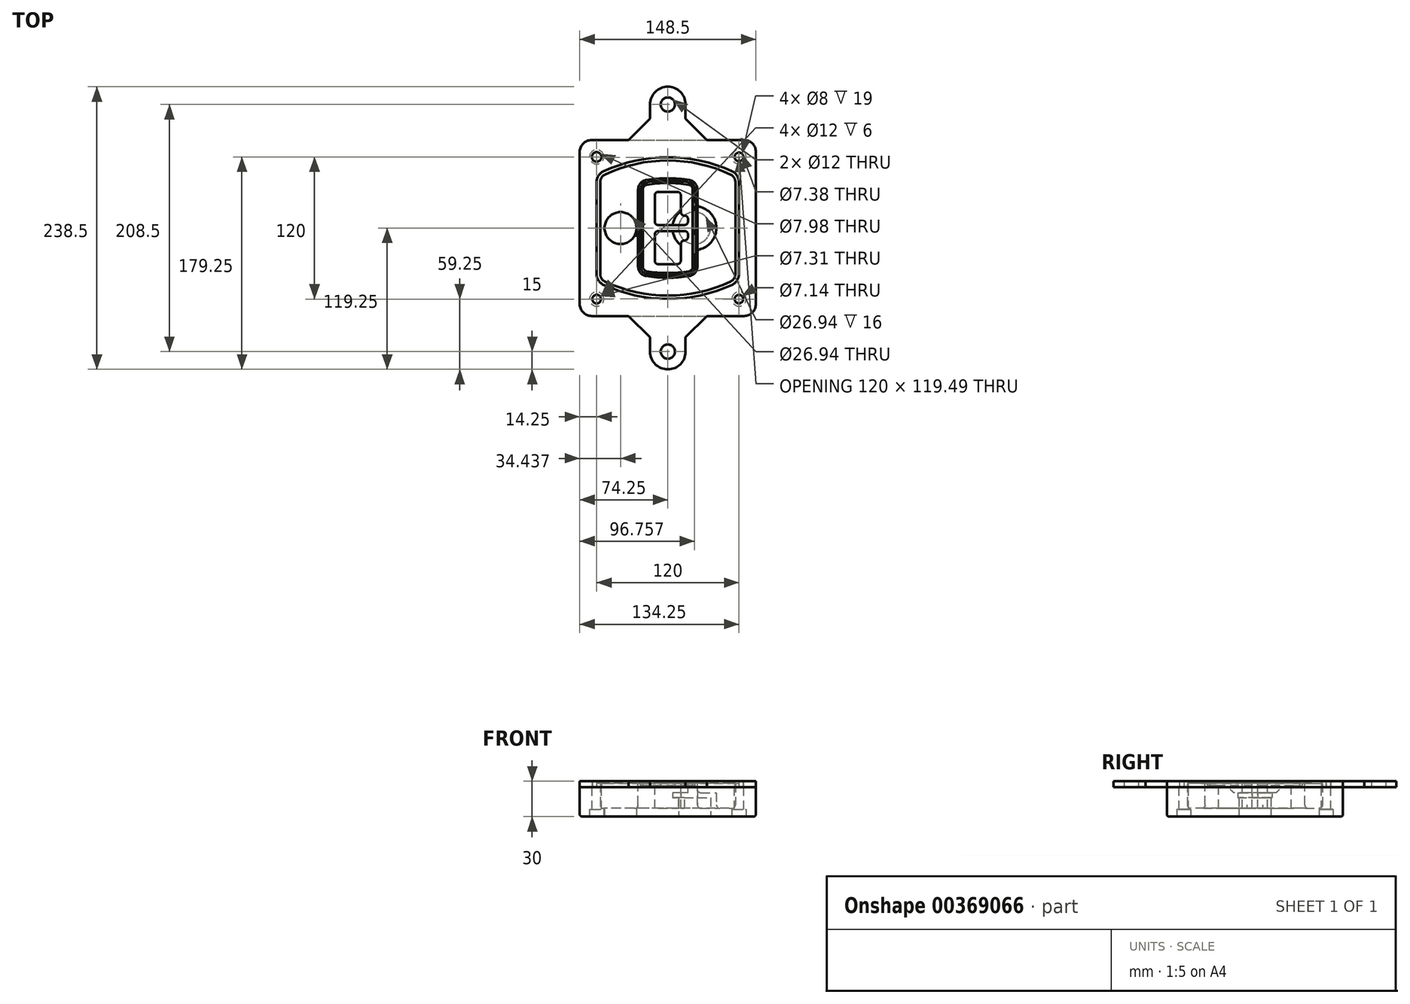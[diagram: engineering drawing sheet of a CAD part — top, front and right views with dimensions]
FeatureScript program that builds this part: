
annotation { "Feature Type Name" : "Feature", "Feature Type Description" : "" }
export const myFeature = defineFeature(function(context is Context, id is Id, definition is map)
    precondition{}
    {
        {
            var Q0;
            Q0=qCreatedBy(makeId("Top.planeOp"),FACE);
            var sketch = newSketch(context, id + "F0", { "sketchPlane" : qUnion([Q0])});
            skPoint(sketch, "E0.rect.middle", {"position": v(0, 0) * mm});
            skLineSegment(sketch, "E1.bottom", {"start": v(-64.25, -74.25) * mm, "end": v(64.25, -74.25) * mm});
            skLineSegment(sketch, "E1.top", {"start": v(-64.25, 74.25) * mm, "end": v(64.25, 74.25) * mm});
            skLineSegment(sketch, "E1.left", {"start": v(-74.25, -64.25) * mm, "end": v(-74.25, 64.25) * mm});
            skLineSegment(sketch, "E1.right", {"start": v(74.25, -64.25) * mm, "end": v(74.25, 64.25) * mm});
            skLineSegment(sketch, "E2", {"start": v(-74.25, 74.25) * mm, "end": v(74.25, -74.25) * mm, "construction": true});
            skLineSegment(sketch, "E3", {"start": v(74.25, 74.25) * mm, "end": v(-74.25, -74.25) * mm, "construction": true});
            skCircle(sketch, "E4", {"center": v(-60, 60) * mm, "radius": 4 * mm});
            skCircle(sketch, "E5", {"center": v(60, 60) * mm, "radius": 4 * mm});
            skCircle(sketch, "E6", {"center": v(60, -60) * mm, "radius": 4 * mm});
            skCircle(sketch, "E7", {"center": v(-60, -60) * mm, "radius": 4 * mm});
            skLineSegment(sketch, "E8", {"start": v(-60, 60) * mm, "end": v(60, 60) * mm, "construction": true});
            skLineSegment(sketch, "E9", {"start": v(60, 60) * mm, "end": v(60, -60) * mm, "construction": true});
            skLineSegment(sketch, "E10", {"start": v(60, -60) * mm, "end": v(-60, -60) * mm, "construction": true});
            skLineSegment(sketch, "E11", {"start": v(-60, -60) * mm, "end": v(-60, 60) * mm, "construction": true});
            skLineSegment(sketch, "E12", {"start": v(-60, 38.83) * mm, "end": v(-60, -38.83) * mm});
            skLineSegment(sketch, "E13", {"start": v(60, 38.83) * mm, "end": v(60, -38.83) * mm});
            skArc(sketch, "E14", {"start": v(54.26, 47.88) * mm, "mid": v(0, 60) * mm, "end": v(-54.26, 47.88) * mm});
            skArc(sketch, "E15", {"start": v(-54.26, -47.88) * mm, "mid": v(0, -60) * mm, "end": v(54.26, -47.88) * mm});
            skLineSegment(sketch, "E16", {"start": v(-60, 0) * mm, "end": v(60, 0) * mm, "construction": true});
            skPoint(sketch, "E17.visualSharp", {"position": v(-60, -45) * mm});
            skArc(sketch, "E17.filletArc", {"start": v(-60, -38.83) * mm, "mid": v(-58.44, -44.2) * mm, "end": v(-54.26, -47.88) * mm});
            skPoint(sketch, "E18.visualSharp", {"position": v(-60, 45) * mm});
            skArc(sketch, "E18.filletArc", {"start": v(-54.26, 47.88) * mm, "mid": v(-58.44, 44.2) * mm, "end": v(-60, 38.83) * mm});
            skPoint(sketch, "E19.visualSharp", {"position": v(60, 45) * mm});
            skArc(sketch, "E19.filletArc", {"start": v(60, 38.83) * mm, "mid": v(58.44, 44.2) * mm, "end": v(54.26, 47.88) * mm});
            skPoint(sketch, "E20.visualSharp", {"position": v(60, -45) * mm});
            skArc(sketch, "E20.filletArc", {"start": v(54.26, -47.88) * mm, "mid": v(58.44, -44.2) * mm, "end": v(60, -38.83) * mm});
            skPoint(sketch, "E21.visualSharp", {"position": v(-74.25, 74.25) * mm});
            skArc(sketch, "E21.filletArc", {"start": v(-64.25, 74.25) * mm, "mid": v(-71.32, 71.32) * mm, "end": v(-74.25, 64.25) * mm});
            skPoint(sketch, "E22.visualSharp", {"position": v(74.25, 74.25) * mm});
            skArc(sketch, "E22.filletArc", {"start": v(74.25, 64.25) * mm, "mid": v(71.32, 71.32) * mm, "end": v(64.25, 74.25) * mm});
            skPoint(sketch, "E23.visualSharp", {"position": v(74.25, -74.25) * mm});
            skArc(sketch, "E23.filletArc", {"start": v(64.25, -74.25) * mm, "mid": v(71.32, -71.32) * mm, "end": v(74.25, -64.25) * mm});
            skPoint(sketch, "E24.visualSharp", {"position": v(-74.25, -74.25) * mm});
            skArc(sketch, "E24.filletArc", {"start": v(-74.25, -64.25) * mm, "mid": v(-71.32, -71.32) * mm, "end": v(-64.25, -74.25) * mm});
            skArc(sketch, "E25.0", {"start": v(57, 38.83) * mm, "mid": v(55.9, 42.58) * mm, "end": v(52.98, 45.17) * mm});
            skLineSegment(sketch, "E25.1", {"start": v(57, 38.83) * mm, "end": v(57, -38.83) * mm});
            skArc(sketch, "E25.2", {"start": v(52.98, -45.17) * mm, "mid": v(55.9, -42.58) * mm, "end": v(57, -38.83) * mm});
            skArc(sketch, "E25.3", {"start": v(-52.98, -45.17) * mm, "mid": v(0, -57) * mm, "end": v(52.98, -45.17) * mm});
            skArc(sketch, "E25.4", {"start": v(-57, -38.83) * mm, "mid": v(-55.9, -42.58) * mm, "end": v(-52.98, -45.17) * mm});
            skArc(sketch, "E25.5", {"start": v(52.98, 45.17) * mm, "mid": v(0, 57) * mm, "end": v(-52.98, 45.17) * mm});
            skLineSegment(sketch, "E25.6", {"start": v(-57, 38.83) * mm, "end": v(-57, -38.83) * mm});
            skArc(sketch, "E25.7", {"start": v(-52.98, 45.17) * mm, "mid": v(-55.9, 42.58) * mm, "end": v(-57, 38.83) * mm});
            skArc(sketch, "E26.0", {"start": v(-55.96, 51.5) * mm, "mid": v(-61.82, 46.33) * mm, "end": v(-64, 38.83) * mm});
            skArc(sketch, "E26.1", {"start": v(55.96, 51.5) * mm, "mid": v(0, 64) * mm, "end": v(-55.96, 51.5) * mm});
            skArc(sketch, "E26.2", {"start": v(64, 38.83) * mm, "mid": v(61.82, 46.33) * mm, "end": v(55.96, 51.5) * mm});
            skLineSegment(sketch, "E26.3", {"start": v(64, 38.83) * mm, "end": v(64, -38.83) * mm});
            skArc(sketch, "E26.4", {"start": v(55.96, -51.5) * mm, "mid": v(61.82, -46.33) * mm, "end": v(64, -38.83) * mm});
            skLineSegment(sketch, "E26.5", {"start": v(-64, 38.83) * mm, "end": v(-64, -38.83) * mm});
            skArc(sketch, "E26.6", {"start": v(-55.96, -51.5) * mm, "mid": v(0, -64) * mm, "end": v(55.96, -51.5) * mm});
            skArc(sketch, "E26.7", {"start": v(-64, -38.83) * mm, "mid": v(-61.82, -46.33) * mm, "end": v(-55.96, -51.5) * mm});
            skSolve(sketch);
        }
        {
            var Q0;
            Q0=makeQuery(id+"F0.imprint","IMPRINT",FACE,{"disambiguationData":[TD([[makeQuery(id+"F0.imprint","IMPRINT",EDGE,{"derivedFrom":sQuery(id+"F0.wireOp",EDGE,"E1.bottom")}),1.0]])]});
            var Q1;
            Q1=makeQuery(id+"F0.imprint","IMPRINT",FACE,{"disambiguationData":[TD([[makeQuery(id+"F0.imprint","IMPRINT",EDGE,{"derivedFrom":sQuery(id+"F0.wireOp",EDGE,"E12")}),1.0]])]});
            var Q2;
            Q2=makeQuery(id+"F0.imprint","IMPRINT",FACE,{"disambiguationData":[TD([[makeQuery(id+"F0.imprint","IMPRINT",EDGE,{"derivedFrom":sQuery(id+"F0.wireOp",EDGE,"E25.0")}),1.0]])]});
            var Q3;
            Q3=makeQuery(id+"F0.imprint","IMPRINT",FACE,{"disambiguationData":[TD([[makeQuery(id+"F0.imprint","IMPRINT",EDGE,{"derivedFrom":sQuery(id+"F0.wireOp",EDGE,"E12")}),-1.0]])]});
            extrude(context, id + "F1", {"entities" : qUnion([Q0, Q1, Q2, Q3]), "oppositeDirection" : true, "depth" : 25 * mm});
        }
        {
            var Q0;
            Q0=makeQuery(id+"F0.imprint","IMPRINT",FACE,{"disambiguationData":[TD([[makeQuery(id+"F0.imprint","IMPRINT",EDGE,{"derivedFrom":sQuery(id+"F0.wireOp",EDGE,"E12")}),1.0]])]});
            extrude(context, id + "F2", {"entities" : qUnion([Q0]), "operationType" : NewBodyOperationType.ADD, "depth" : 3 * mm});
        }
        {
            var Q0;
            Q0=makeQuery(id+"F0.imprint","IMPRINT",FACE,{"disambiguationData":[TD([[makeQuery(id+"F0.imprint","IMPRINT",EDGE,{"derivedFrom":sQuery(id+"F0.wireOp",EDGE,"E25.0")}),1.0]])]});
            extrude(context, id + "F3", {"entities" : qUnion([Q0]), "operationType" : NewBodyOperationType.REMOVE, "oppositeDirection" : true, "depth" : 18 * mm});
        }
        {
            var Q0;
            Q0=makeQuery(id+"F2.opExtrude","CAP_FACE",FACE,{"disambiguationData":[OSD([sQuery(id+"F0.wireOp",EDGE,"E12"),sQuery(id+"F0.wireOp",EDGE,"E13"),sQuery(id+"F0.wireOp",EDGE,"E14"),sQuery(id+"F0.wireOp",EDGE,"E15"),sQuery(id+"F0.wireOp",EDGE,"E17.filletArc"),sQuery(id+"F0.wireOp",EDGE,"E18.filletArc"),sQuery(id+"F0.wireOp",EDGE,"E19.filletArc"),sQuery(id+"F0.wireOp",EDGE,"E20.filletArc"),sQuery(id+"F0.wireOp",EDGE,"E25.0"),sQuery(id+"F0.wireOp",EDGE,"E25.1"),sQuery(id+"F0.wireOp",EDGE,"E25.2"),sQuery(id+"F0.wireOp",EDGE,"E25.3"),sQuery(id+"F0.wireOp",EDGE,"E25.4"),sQuery(id+"F0.wireOp",EDGE,"E25.5"),sQuery(id+"F0.wireOp",EDGE,"E25.6"),sQuery(id+"F0.wireOp",EDGE,"E25.7")])],"isStart":false});
            var sketch = newSketch(context, id + "F4", { "sketchPlane" : qUnion([Q0])});
            skArc(sketch, "E27.0", {"start": v(-18.34, -40.45) * mm, "mid": v(0, -42) * mm, "end": v(18.34, -40.45) * mm});
            skArc(sketch, "E28.0", {"start": v(18.34, 40.45) * mm, "mid": v(0, 42) * mm, "end": v(-18.34, 40.45) * mm});
            skLineSegment(sketch, "E29", {"start": v(-25, 32.57) * mm, "end": v(-25, -32.57) * mm});
            skLineSegment(sketch, "E30", {"start": v(25, 32.57) * mm, "end": v(25, -32.57) * mm});
            skLineSegment(sketch, "E31", {"start": v(-25, 39.1) * mm, "end": v(25, 39.1) * mm, "construction": true});
            skLineSegment(sketch, "E32", {"start": v(-25, -39.1) * mm, "end": v(25, -39.1) * mm, "construction": true});
            skPoint(sketch, "E33.visualSharp", {"position": v(-25, 39.1) * mm});
            skArc(sketch, "E33.filletArc", {"start": v(-18.34, 40.45) * mm, "mid": v(-23.11, 37.73) * mm, "end": v(-25, 32.57) * mm});
            skPoint(sketch, "E34.visualSharp", {"position": v(25, 39.1) * mm});
            skArc(sketch, "E34.filletArc", {"start": v(25, 32.57) * mm, "mid": v(23.11, 37.73) * mm, "end": v(18.34, 40.45) * mm});
            skPoint(sketch, "E35.visualSharp", {"position": v(25, -39.1) * mm});
            skArc(sketch, "E35.filletArc", {"start": v(18.34, -40.45) * mm, "mid": v(23.11, -37.73) * mm, "end": v(25, -32.57) * mm});
            skPoint(sketch, "E36.visualSharp", {"position": v(-25, -39.1) * mm});
            skArc(sketch, "E36.filletArc", {"start": v(-25, -32.57) * mm, "mid": v(-23.11, -37.73) * mm, "end": v(-18.34, -40.45) * mm});
            skArc(sketch, "E37.0", {"start": v(52.98, 45.17) * mm, "mid": v(0, 57) * mm, "end": v(-52.98, 45.17) * mm});
            skArc(sketch, "E37.1", {"start": v(-52.98, 45.17) * mm, "mid": v(-55.9, 42.58) * mm, "end": v(-57, 38.83) * mm});
            skLineSegment(sketch, "E37.2", {"start": v(-57, 38.83) * mm, "end": v(-57, -38.83) * mm});
            skArc(sketch, "E37.3", {"start": v(-57, -38.83) * mm, "mid": v(-55.9, -42.58) * mm, "end": v(-52.98, -45.17) * mm});
            skArc(sketch, "E37.4", {"start": v(-52.98, -45.17) * mm, "mid": v(0, -57) * mm, "end": v(52.98, -45.17) * mm});
            skArc(sketch, "E37.5", {"start": v(52.98, -45.17) * mm, "mid": v(55.9, -42.58) * mm, "end": v(57, -38.83) * mm});
            skLineSegment(sketch, "E37.6", {"start": v(57, 38.83) * mm, "end": v(57, -38.83) * mm});
            skArc(sketch, "E37.7", {"start": v(57, 38.83) * mm, "mid": v(55.9, 42.58) * mm, "end": v(52.98, 45.17) * mm});
            skLineSegment(sketch, "E38.0", {"start": v(23, 32.57) * mm, "end": v(23, -32.57) * mm});
            skArc(sketch, "E38.1", {"start": v(18, -38.48) * mm, "mid": v(21.58, -36.44) * mm, "end": v(23, -32.57) * mm});
            skArc(sketch, "E38.2", {"start": v(-18, -38.48) * mm, "mid": v(0, -40) * mm, "end": v(18, -38.48) * mm});
            skArc(sketch, "E38.3", {"start": v(-23, -32.57) * mm, "mid": v(-21.58, -36.44) * mm, "end": v(-18, -38.48) * mm});
            skLineSegment(sketch, "E38.4", {"start": v(-23, 32.57) * mm, "end": v(-23, -32.57) * mm});
            skArc(sketch, "E38.5", {"start": v(23, 32.57) * mm, "mid": v(21.58, 36.44) * mm, "end": v(18, 38.48) * mm});
            skArc(sketch, "E38.6", {"start": v(-18, 38.48) * mm, "mid": v(-21.58, 36.44) * mm, "end": v(-23, 32.57) * mm});
            skArc(sketch, "E38.7", {"start": v(18, 38.48) * mm, "mid": v(0, 40) * mm, "end": v(-18, 38.48) * mm});
            skArc(sketch, "E39.0", {"start": v(21, 32.57) * mm, "mid": v(20.06, 35.15) * mm, "end": v(17.67, 36.5) * mm});
            skLineSegment(sketch, "E39.1", {"start": v(21, 32.57) * mm, "end": v(21, -32.57) * mm});
            skArc(sketch, "E39.2", {"start": v(17.67, -36.5) * mm, "mid": v(20.06, -35.15) * mm, "end": v(21, -32.57) * mm});
            skArc(sketch, "E39.3", {"start": v(-17.67, -36.5) * mm, "mid": v(0, -38) * mm, "end": v(17.67, -36.5) * mm});
            skArc(sketch, "E39.4", {"start": v(-21, -32.57) * mm, "mid": v(-20.06, -35.15) * mm, "end": v(-17.67, -36.5) * mm});
            skArc(sketch, "E39.5", {"start": v(17.67, 36.5) * mm, "mid": v(0, 38) * mm, "end": v(-17.67, 36.5) * mm});
            skLineSegment(sketch, "E39.6", {"start": v(-21, 32.57) * mm, "end": v(-21, -32.57) * mm});
            skArc(sketch, "E39.7", {"start": v(-17.67, 36.5) * mm, "mid": v(-20.06, 35.15) * mm, "end": v(-21, 32.57) * mm});
            skLineSegment(sketch, "E40", {"start": v(-25, 0) * mm, "end": v(25, 0) * mm, "construction": true});
            skLineSegment(sketch, "E41", {"start": v(-11, 5.5) * mm, "end": v(-11, 27.5) * mm});
            skLineSegment(sketch, "E42", {"start": v(-8, 30.5) * mm, "end": v(8, 30.5) * mm});
            skLineSegment(sketch, "E43", {"start": v(11, 27.5) * mm, "end": v(11, 13.5) * mm});
            skLineSegment(sketch, "E44", {"start": v(14, 10.5) * mm, "end": v(14, 10.5) * mm});
            skLineSegment(sketch, "E45", {"start": v(17, 7.5) * mm, "end": v(17, 5.5) * mm});
            skLineSegment(sketch, "E46", {"start": v(14, 2.5) * mm, "end": v(-8, 2.5) * mm});
            skPoint(sketch, "E47.visualSharp", {"position": v(-11, 30.5) * mm});
            skArc(sketch, "E47.filletArc", {"start": v(-8, 30.5) * mm, "mid": v(-10.12, 29.62) * mm, "end": v(-11, 27.5) * mm});
            skPoint(sketch, "E48.visualSharp", {"position": v(11, 30.5) * mm});
            skArc(sketch, "E48.filletArc", {"start": v(11, 27.5) * mm, "mid": v(10.12, 29.62) * mm, "end": v(8, 30.5) * mm});
            skPoint(sketch, "E49.visualSharp", {"position": v(11, 10.5) * mm});
            skArc(sketch, "E49.filletArc", {"start": v(11, 13.5) * mm, "mid": v(11.88, 11.38) * mm, "end": v(14, 10.5) * mm});
            skPoint(sketch, "E50.visualSharp", {"position": v(17, 10.5) * mm});
            skArc(sketch, "E50.filletArc", {"start": v(17, 7.5) * mm, "mid": v(16.12, 9.62) * mm, "end": v(14, 10.5) * mm});
            skPoint(sketch, "E51.visualSharp", {"position": v(17, 2.5) * mm});
            skArc(sketch, "E51.filletArc", {"start": v(14, 2.5) * mm, "mid": v(16.12, 3.38) * mm, "end": v(17, 5.5) * mm});
            skPoint(sketch, "E52.visualSharp", {"position": v(-11, 2.5) * mm});
            skArc(sketch, "E52.filletArc", {"start": v(-11, 5.5) * mm, "mid": v(-10.12, 3.38) * mm, "end": v(-8, 2.5) * mm});
            skLineSegment(sketch, "E53.0.MirrorCS", {"start": v(14, -2.5) * mm, "end": v(-8, -2.5) * mm});
            skArc(sketch, "E54.0.MirrorCS", {"start": v(-11, -5.5) * mm, "mid": v(-10.12, -3.38) * mm, "end": v(-8, -2.5) * mm});
            skLineSegment(sketch, "E55.0.MirrorCS", {"start": v(-11, -5.5) * mm, "end": v(-11, -27.5) * mm});
            skArc(sketch, "E56.0.MirrorCS", {"start": v(-8, -30.5) * mm, "mid": v(-10.12, -29.62) * mm, "end": v(-11, -27.5) * mm});
            skLineSegment(sketch, "E57.0.MirrorCS", {"start": v(-8, -30.5) * mm, "end": v(8, -30.5) * mm});
            skArc(sketch, "E58.0.MirrorCS", {"start": v(11, -27.5) * mm, "mid": v(10.12, -29.62) * mm, "end": v(8, -30.5) * mm});
            skLineSegment(sketch, "E59.0.MirrorCS", {"start": v(11, -27.5) * mm, "end": v(11, -13.5) * mm});
            skArc(sketch, "E60.0.MirrorCS", {"start": v(11, -13.5) * mm, "mid": v(11.88, -11.38) * mm, "end": v(14, -10.5) * mm});
            skArc(sketch, "E61.0.MirrorCS", {"start": v(17, -7.5) * mm, "mid": v(16.12, -9.62) * mm, "end": v(14, -10.5) * mm});
            skLineSegment(sketch, "E62.0.MirrorCS", {"start": v(17, -7.5) * mm, "end": v(17, -5.5) * mm});
            skArc(sketch, "E63.0.MirrorCS", {"start": v(14, -2.5) * mm, "mid": v(16.12, -3.38) * mm, "end": v(17, -5.5) * mm});
            skSolve(sketch);
        }
        {
            var Q0;
            Q0=makeQuery(id+"F4.imprint","IMPRINT",FACE,{"disambiguationData":[TD([[makeQuery(id+"F4.imprint","IMPRINT",EDGE,{"derivedFrom":sQuery(id+"F4.wireOp",EDGE,"E27.0")}),1.0]])]});
            var Q1;
            Q1=makeQuery(id+"F4.imprint","IMPRINT",FACE,{"disambiguationData":[TD([[makeQuery(id+"F4.imprint","IMPRINT",EDGE,{"derivedFrom":sQuery(id+"F4.wireOp",EDGE,"E38.0")}),-1.0]])]});
            var Q2;
            Q2=makeQuery(id+"F4.imprint","IMPRINT",FACE,{"disambiguationData":[TD([[makeQuery(id+"F4.imprint","IMPRINT",EDGE,{"derivedFrom":sQuery(id+"F4.wireOp",EDGE,"E39.0")}),1.0]])]});
            extrude(context, id + "F5", {"entities" : qUnion([Q0, Q1, Q2]), "operationType" : NewBodyOperationType.ADD, "endBound" : BoundingType.UP_TO_NEXT, "oppositeDirection" : true, "depth" : 25 * mm});
        }
        {
            var Q0;
            Q0=makeQuery(id+"F4.imprint","IMPRINT",FACE,{"disambiguationData":[TD([[makeQuery(id+"F4.imprint","IMPRINT",EDGE,{"derivedFrom":sQuery(id+"F4.wireOp",EDGE,"E38.0")}),-1.0]])]});
            extrude(context, id + "F6", {"entities" : qUnion([Q0]), "operationType" : NewBodyOperationType.REMOVE, "oppositeDirection" : true, "depth" : 2 * mm});
        }
        {
            var Q0;
            Q0=makeQuery(id+"F1.opExtrude","CAP_FACE",FACE,{"disambiguationData":[OSD([sQuery(id+"F0.wireOp",EDGE,"E1.bottom"),sQuery(id+"F0.wireOp",EDGE,"E1.top"),sQuery(id+"F0.wireOp",EDGE,"E1.left"),sQuery(id+"F0.wireOp",EDGE,"E1.right"),sQuery(id+"F0.wireOp",EDGE,"E4"),sQuery(id+"F0.wireOp",EDGE,"E5"),sQuery(id+"F0.wireOp",EDGE,"E6"),sQuery(id+"F0.wireOp",EDGE,"E7"),sQuery(id+"F0.wireOp",EDGE,"E21.filletArc"),sQuery(id+"F0.wireOp",EDGE,"E22.filletArc"),sQuery(id+"F0.wireOp",EDGE,"E23.filletArc"),sQuery(id+"F0.wireOp",EDGE,"E24.filletArc")])],"isStart":false});
            var sketch = newSketch(context, id + "F7", { "sketchPlane" : qUnion([Q0])});
            skCircle(sketch, "E64", {"center": v(22.5, 0) * mm, "radius": 13.47 * mm});
            skCircle(sketch, "E65", {"center": v(-39.81, 0) * mm, "radius": 13.47 * mm});
            skLineSegment(sketch, "E66", {"start": v(74.25, 0) * mm, "end": v(-74.25, 0) * mm});
            skCircle(sketch, "E67", {"center": v(22.5, 0) * mm, "radius": 18.47 * mm});
            skCircle(sketch, "E68", {"center": v(60, -60) * mm, "radius": 6 * mm});
            skCircle(sketch, "E69", {"center": v(-60, -60) * mm, "radius": 6 * mm});
            skCircle(sketch, "E70", {"center": v(-60, 60) * mm, "radius": 6 * mm});
            skCircle(sketch, "E71", {"center": v(60, 60) * mm, "radius": 6 * mm});
            skSolve(sketch);
        }
        {
            var Q0;
            {var subQ1=sQuery(id+"F7.wireOp",EDGE,"E66");var subQ4=sQuery(id+"F7.wireOp",EDGE,"E64");var subQ6=makeQuery(id+"F7.imprint","INTERSECT",VERTEX,{"disambiguationData":[OD(0.0)],"derivedFrom":[subQ4,subQ1]});Q0=makeQuery(id+"F7.imprint","IMPRINT",FACE,{"disambiguationData":[TD([[makeQuery(id+"F7.imprint","IMPRINT",EDGE,{"disambiguationData":[TD([[subQ6,-1.0]])],"derivedFrom":subQ4}),-1.0]])]});}
            var Q1;
            {var subQ0=sQuery(id+"F7.wireOp",EDGE,"E66");var subQ1=sQuery(id+"F7.wireOp",EDGE,"E64");var subQ3=makeQuery(id+"F7.imprint","INTERSECT",VERTEX,{"disambiguationData":[OD(0.0)],"derivedFrom":[subQ1,subQ0]});Q1=makeQuery(id+"F7.imprint","IMPRINT",FACE,{"disambiguationData":[TD([[makeQuery(id+"F7.imprint","IMPRINT",EDGE,{"disambiguationData":[TD([[subQ3,-1.0]])],"derivedFrom":subQ1}),1.0]])]});}
            var Q2;
            {var subQ0=sQuery(id+"F7.wireOp",EDGE,"E66");var subQ1=sQuery(id+"F7.wireOp",EDGE,"E64");var subQ3=makeQuery(id+"F7.imprint","INTERSECT",VERTEX,{"disambiguationData":[OD(0.0)],"derivedFrom":[subQ1,subQ0]});Q2=makeQuery(id+"F7.imprint","IMPRINT",FACE,{"disambiguationData":[TD([[makeQuery(id+"F7.imprint","IMPRINT",EDGE,{"disambiguationData":[TD([[subQ3,1.0]])],"derivedFrom":subQ1}),1.0]])]});}
            var Q3;
            {var subQ1=sQuery(id+"F7.wireOp",EDGE,"E66");var subQ4=sQuery(id+"F7.wireOp",EDGE,"E64");var subQ6=makeQuery(id+"F7.imprint","INTERSECT",VERTEX,{"disambiguationData":[OD(0.0)],"derivedFrom":[subQ4,subQ1]});Q3=makeQuery(id+"F7.imprint","IMPRINT",FACE,{"disambiguationData":[TD([[makeQuery(id+"F7.imprint","IMPRINT",EDGE,{"disambiguationData":[TD([[subQ6,1.0]])],"derivedFrom":subQ4}),-1.0]])]});}
            extrude(context, id + "F8", {"entities" : qUnion([Q0, Q1, Q2, Q3]), "operationType" : NewBodyOperationType.ADD, "oppositeDirection" : true, "depth" : 20 * mm});
        }
        {
            var Q0;
            {var subQ0=sQuery(id+"F7.wireOp",EDGE,"E66");var subQ1=sQuery(id+"F7.wireOp",EDGE,"E64");var subQ3=makeQuery(id+"F7.imprint","INTERSECT",VERTEX,{"disambiguationData":[OD(0.0)],"derivedFrom":[subQ1,subQ0]});Q0=makeQuery(id+"F7.imprint","IMPRINT",FACE,{"disambiguationData":[TD([[makeQuery(id+"F7.imprint","IMPRINT",EDGE,{"disambiguationData":[TD([[subQ3,-1.0]])],"derivedFrom":subQ1}),1.0]])]});}
            var Q1;
            {var subQ0=sQuery(id+"F7.wireOp",EDGE,"E66");var subQ1=sQuery(id+"F7.wireOp",EDGE,"E64");var subQ3=makeQuery(id+"F7.imprint","INTERSECT",VERTEX,{"disambiguationData":[OD(0.0)],"derivedFrom":[subQ1,subQ0]});Q1=makeQuery(id+"F7.imprint","IMPRINT",FACE,{"disambiguationData":[TD([[makeQuery(id+"F7.imprint","IMPRINT",EDGE,{"disambiguationData":[TD([[subQ3,1.0]])],"derivedFrom":subQ1}),1.0]])]});}
            extrude(context, id + "F9", {"entities" : qUnion([Q0, Q1]), "operationType" : NewBodyOperationType.REMOVE, "oppositeDirection" : true, "depth" : 16 * mm});
        }
        {
            var Q0;
            {var subQ0=sQuery(id+"F7.wireOp",EDGE,"E66");var subQ1=sQuery(id+"F7.wireOp",EDGE,"E65");var subQ3=makeQuery(id+"F7.imprint","INTERSECT",VERTEX,{"disambiguationData":[OD(0.0)],"derivedFrom":[subQ1,subQ0]});Q0=makeQuery(id+"F7.imprint","IMPRINT",FACE,{"disambiguationData":[TD([[makeQuery(id+"F7.imprint","IMPRINT",EDGE,{"disambiguationData":[TD([[subQ3,-1.0]])],"derivedFrom":subQ1}),1.0]])]});}
            var Q1;
            {var subQ0=sQuery(id+"F7.wireOp",EDGE,"E66");var subQ1=sQuery(id+"F7.wireOp",EDGE,"E65");var subQ3=makeQuery(id+"F7.imprint","INTERSECT",VERTEX,{"disambiguationData":[OD(0.0)],"derivedFrom":[subQ1,subQ0]});Q1=makeQuery(id+"F7.imprint","IMPRINT",FACE,{"disambiguationData":[TD([[makeQuery(id+"F7.imprint","IMPRINT",EDGE,{"disambiguationData":[TD([[subQ3,1.0]])],"derivedFrom":subQ1}),1.0]])]});}
            extrude(context, id + "F10", {"entities" : qUnion([Q0, Q1]), "operationType" : NewBodyOperationType.REMOVE, "oppositeDirection" : true, "depth" : 25 * mm});
        }
        {
            var Q0;
            Q0=makeQuery(id+"F7.imprint","IMPRINT",FACE,{"disambiguationData":[TD([[makeQuery(id+"F7.imprint","IMPRINT",EDGE,{"derivedFrom":sQuery(id+"F7.wireOp",EDGE,"E68")}),1.0]])]});
            var Q1;
            Q1=makeQuery(id+"F7.imprint","IMPRINT",FACE,{"disambiguationData":[TD([[makeQuery(id+"F7.imprint","IMPRINT",EDGE,{"derivedFrom":makeQuery(id+"F1.opExtrude","CAP_EDGE",EDGE,{"disambiguationData":[OSD([sQuery(id+"F0.wireOp",EDGE,"E5")])],"isStart":false})}),-1.0]])]});
            var Q2;
            Q2=makeQuery(id+"F7.imprint","IMPRINT",FACE,{"disambiguationData":[TD([[makeQuery(id+"F7.imprint","IMPRINT",EDGE,{"derivedFrom":sQuery(id+"F7.wireOp",EDGE,"E69")}),1.0]])]});
            var Q3;
            Q3=makeQuery(id+"F7.imprint","IMPRINT",FACE,{"disambiguationData":[TD([[makeQuery(id+"F7.imprint","IMPRINT",EDGE,{"derivedFrom":makeQuery(id+"F1.opExtrude","CAP_EDGE",EDGE,{"disambiguationData":[OSD([sQuery(id+"F0.wireOp",EDGE,"E4")])],"isStart":false})}),-1.0]])]});
            var Q4;
            Q4=makeQuery(id+"F7.imprint","IMPRINT",FACE,{"disambiguationData":[TD([[makeQuery(id+"F7.imprint","IMPRINT",EDGE,{"derivedFrom":sQuery(id+"F7.wireOp",EDGE,"E70")}),1.0]])]});
            var Q5;
            Q5=makeQuery(id+"F7.imprint","IMPRINT",FACE,{"disambiguationData":[TD([[makeQuery(id+"F7.imprint","IMPRINT",EDGE,{"derivedFrom":makeQuery(id+"F1.opExtrude","CAP_EDGE",EDGE,{"disambiguationData":[OSD([sQuery(id+"F0.wireOp",EDGE,"E7")])],"isStart":false})}),-1.0]])]});
            var Q6;
            Q6=makeQuery(id+"F7.imprint","IMPRINT",FACE,{"disambiguationData":[TD([[makeQuery(id+"F7.imprint","IMPRINT",EDGE,{"derivedFrom":sQuery(id+"F7.wireOp",EDGE,"E71")}),1.0]])]});
            var Q7;
            Q7=makeQuery(id+"F7.imprint","IMPRINT",FACE,{"disambiguationData":[TD([[makeQuery(id+"F7.imprint","IMPRINT",EDGE,{"derivedFrom":makeQuery(id+"F1.opExtrude","CAP_EDGE",EDGE,{"disambiguationData":[OSD([sQuery(id+"F0.wireOp",EDGE,"E6")])],"isStart":false})}),-1.0]])]});
            extrude(context, id + "F11", {"entities" : qUnion([Q0, Q1, Q2, Q3, Q4, Q5, Q6, Q7]), "operationType" : NewBodyOperationType.REMOVE, "oppositeDirection" : true, "depth" : 6 * mm});
        }
        {
            var Q0;
            Q0=makeQuery(id+"F9.boolean.opBoolean","COPY",FACE,{"derivedFrom":makeQuery(id+"F9.opExtrude","CAP_FACE",FACE,{"disambiguationData":[OSD([sQuery(id+"F7.wireOp",EDGE,"E64")])],"isStart":false})});
            var sketch = newSketch(context, id + "F12", { "sketchPlane" : qUnion([Q0])});
            skArc(sketch, "E72.0", {"start": v(11, 14.45) * mm, "mid": v(6.45, 9.13) * mm, "end": v(4.2, 2.5) * mm});
            skArc(sketch, "E72.1", {"start": v(4.2, -2.5) * mm, "mid": v(6.45, -9.13) * mm, "end": v(11, -14.45) * mm});
            skLineSegment(sketch, "E73", {"start": v(4.2, -2.5) * mm, "end": v(14, -2.5) * mm});
            skLineSegment(sketch, "E74.0", {"start": v(14, 2.5) * mm, "end": v(4.2, 2.5) * mm});
            skArc(sketch, "E74.1", {"start": v(14, 2.5) * mm, "mid": v(16.12, 3.38) * mm, "end": v(17, 5.5) * mm});
            skLineSegment(sketch, "E74.2", {"start": v(17, 7.5) * mm, "end": v(17, 5.5) * mm});
            skArc(sketch, "E74.3", {"start": v(17, 7.5) * mm, "mid": v(16.12, 9.62) * mm, "end": v(14, 10.5) * mm});
            skArc(sketch, "E74.4", {"start": v(11, 13.5) * mm, "mid": v(11.88, 11.38) * mm, "end": v(14, 10.5) * mm});
            skLineSegment(sketch, "E74.5", {"start": v(11, 14.45) * mm, "end": v(11, 13.5) * mm});
            skLineSegment(sketch, "E74.7", {"start": v(14, -2.5) * mm, "end": v(4.2, -2.5) * mm});
            skArc(sketch, "E74.8", {"start": v(14, -2.5) * mm, "mid": v(16.12, -3.38) * mm, "end": v(17, -5.5) * mm});
            skLineSegment(sketch, "E74.9", {"start": v(17, -7.5) * mm, "end": v(17, -5.5) * mm});
            skArc(sketch, "E74.10", {"start": v(17, -7.5) * mm, "mid": v(16.12, -9.62) * mm, "end": v(14, -10.5) * mm});
            skArc(sketch, "E74.11", {"start": v(11, -13.5) * mm, "mid": v(11.88, -11.38) * mm, "end": v(14, -10.5) * mm});
            skLineSegment(sketch, "E74.12", {"start": v(11, -14.45) * mm, "end": v(11, -13.5) * mm});
            skPoint(sketch, "E75.orphan", {"position": v(11, -27.5) * mm});
            skPoint(sketch, "E76.orphan", {"position": v(-8, -2.5) * mm});
            skPoint(sketch, "E77.orphan", {"position": v(-8, 2.5) * mm});
            skPoint(sketch, "E78.orphan", {"position": v(11, 27.5) * mm});
            skSolve(sketch);
        }
        {
            var Q0;
            {var subQ7=sQuery(id+"F12.wireOp",EDGE,"E72.0");var subQ14=sQuery(id+"F12.wireOp",EDGE,"E72.1");var subQ16=sQuery(id+"F12.wireOp",EDGE,"E74.1");var subQ18=sQuery(id+"F12.wireOp",EDGE,"E74.8");Q0=qUnion([makeQuery(id+"F12.imprint","IMPRINT",FACE,{"disambiguationData":[TD([[makeQuery(id+"F12.imprint","IMPRINT",EDGE,{"derivedFrom":subQ7}),1.0]])]}),makeQuery(id+"F12.imprint","IMPRINT",FACE,{"disambiguationData":[TD([[makeQuery(id+"F12.imprint","IMPRINT",EDGE,{"derivedFrom":subQ14}),1.0]])]}),makeQuery(id+"F12.imprint","IMPRINT",FACE,{"disambiguationData":[TD([[makeQuery(id+"F12.imprint","IMPRINT",EDGE,{"derivedFrom":subQ16}),1.0]])]}),makeQuery(id+"F12.imprint","IMPRINT",FACE,{"disambiguationData":[TD([[makeQuery(id+"F12.imprint","IMPRINT",EDGE,{"derivedFrom":subQ18}),-1.0]])]})]);}
            var Q1;
            Q1=makeQuery(id+"F5.boolean.opBoolean","SPLIT",FACE,{"disambiguationData":[TD([makeQuery(id+"F5.opExtrude","SWEPT_FACE",FACE,{"disambiguationData":[OSD([sQuery(id+"F4.wireOp",EDGE,"E41")])]})])],"derivedFrom":makeQuery(id+"F3.boolean.opBoolean","COPY",FACE,{"derivedFrom":makeQuery(id+"F3.opExtrude","CAP_FACE",FACE,{"disambiguationData":[OSD([sQuery(id+"F0.wireOp",EDGE,"E25.0"),sQuery(id+"F0.wireOp",EDGE,"E25.1"),sQuery(id+"F0.wireOp",EDGE,"E25.2"),sQuery(id+"F0.wireOp",EDGE,"E25.3"),sQuery(id+"F0.wireOp",EDGE,"E25.4"),sQuery(id+"F0.wireOp",EDGE,"E25.5"),sQuery(id+"F0.wireOp",EDGE,"E25.6"),sQuery(id+"F0.wireOp",EDGE,"E25.7")])],"isStart":false})})});
            extrude(context, id + "F13", {"entities" : qUnion([Q0]), "operationType" : NewBodyOperationType.REMOVE, "endBound" : BoundingType.UP_TO_SURFACE, "endBoundEntityFace" : qUnion([Q1]), "depth" : 25 * mm});
        }
        {
            var Q0;
            Q0=makeQuery(id+"F3.boolean.opBoolean","COPY",EDGE,{"derivedFrom":makeQuery(id+"F3.opExtrude","CAP_EDGE",EDGE,{"disambiguationData":[OSD([sQuery(id+"F0.wireOp",EDGE,"E25.6")])],"isStart":false})});
            var Q1;
            Q1=makeQuery(id+"F8.boolean.opBoolean","INTERSECT",EDGE,{"derivedFrom":[makeQuery(id+"F5.opExtrude","SWEPT_FACE",FACE,{"disambiguationData":[OSD([sQuery(id+"F4.wireOp",EDGE,"E30")])]}),makeQuery(id+"F8.opExtrude","CAP_FACE",FACE,{"disambiguationData":[OSD([sQuery(id+"F7.wireOp",EDGE,"E67")])],"isStart":false})]});
            var Q2;
            Q2=makeQuery(id+"F8.boolean.opBoolean","INTERSECT",EDGE,{"disambiguationData":[OD(1.0)],"derivedFrom":[makeQuery(id+"F5.opExtrude","SWEPT_FACE",FACE,{"disambiguationData":[OSD([sQuery(id+"F4.wireOp",EDGE,"E30")])]}),makeQuery(id+"F8.opExtrude","SWEPT_FACE",FACE,{"disambiguationData":[OSD([sQuery(id+"F7.wireOp",EDGE,"E67")])]})]});
            var Q3;
            {var subQ0=sQuery(id+"F4.wireOp",EDGE,"E30");Q3=makeQuery(id+"F8.boolean.opBoolean","SPLIT",EDGE,{"disambiguationData":[TD([makeQuery(id+"F5.opExtrude","SWEPT_FACE",FACE,{"disambiguationData":[OSD([sQuery(id+"F4.wireOp",EDGE,"E35.filletArc")])]})])],"derivedFrom":makeQuery(id+"F5.opExtrude","CAP_EDGE",EDGE,{"disambiguationData":[OSD([subQ0])],"isStart":false})});}
            var Q4;
            {var subQ0=sQuery(id+"F0.wireOp",EDGE,"E25.7");var subQ1=sQuery(id+"F0.wireOp",EDGE,"E25.1");var subQ2=sQuery(id+"F0.wireOp",EDGE,"E25.6");var subQ3=sQuery(id+"F0.wireOp",EDGE,"E25.5");var subQ4=sQuery(id+"F0.wireOp",EDGE,"E25.4");var subQ5=sQuery(id+"F0.wireOp",EDGE,"E25.0");var subQ6=sQuery(id+"F0.wireOp",EDGE,"E25.2");var subQ7=sQuery(id+"F0.wireOp",EDGE,"E25.3");Q4=makeQuery(id+"F8.boolean.opBoolean","INTERSECT",EDGE,{"derivedFrom":[makeQuery(id+"F5.boolean.opBoolean","SPLIT",FACE,{"disambiguationData":[TD([makeQuery(id+"F2.opExtrude","SWEPT_FACE",FACE,{"disambiguationData":[OSD([subQ5])]})])],"derivedFrom":makeQuery(id+"F3.boolean.opBoolean","COPY",FACE,{"derivedFrom":makeQuery(id+"F3.opExtrude","CAP_FACE",FACE,{"disambiguationData":[OSD([subQ5,subQ1,subQ6,subQ7,subQ4,subQ3,subQ2,subQ0])],"isStart":false})})}),makeQuery(id+"F8.opExtrude","SWEPT_FACE",FACE,{"disambiguationData":[OSD([sQuery(id+"F7.wireOp",EDGE,"E67")])]})]});}
            var Q5;
            Q5=makeQuery(id+"F8.boolean.opBoolean","INTERSECT",EDGE,{"disambiguationData":[OD(0.0)],"derivedFrom":[makeQuery(id+"F5.opExtrude","SWEPT_FACE",FACE,{"disambiguationData":[OSD([sQuery(id+"F4.wireOp",EDGE,"E30")])]}),makeQuery(id+"F8.opExtrude","SWEPT_FACE",FACE,{"disambiguationData":[OSD([sQuery(id+"F7.wireOp",EDGE,"E67")])]})]});
            fillet(context, id + "F14", {"entities" : qUnion([Q0, Q1, Q2, Q3, Q4, Q5]), "radius" : 3 * mm, "tangentPropagation" : true, "allowEdgeOverflow" : false});
        }
        {
            var Q0;
            Q0=makeQuery(id+"F1.opExtrude","CAP_EDGE",EDGE,{"disambiguationData":[OSD([sQuery(id+"F0.wireOp",EDGE,"E1.bottom")])],"isStart":false});
            fillet(context, id + "F15", {"entities" : qUnion([Q0]), "radius" : 2 * mm, "tangentPropagation" : true, "allowEdgeOverflow" : false});
        }
        {
            var Q0;
            {var subQ0=sQuery(id+"F0.wireOp",EDGE,"E21.filletArc");var subQ1=sQuery(id+"F0.wireOp",EDGE,"E7");var subQ2=sQuery(id+"F0.wireOp",EDGE,"E6");var subQ3=sQuery(id+"F0.wireOp",EDGE,"E5");var subQ4=sQuery(id+"F0.wireOp",EDGE,"E4");var subQ5=sQuery(id+"F0.wireOp",EDGE,"E22.filletArc");var subQ6=sQuery(id+"F0.wireOp",EDGE,"E1.bottom");var subQ7=sQuery(id+"F0.wireOp",EDGE,"E1.right");var subQ8=sQuery(id+"F0.wireOp",EDGE,"E1.top");var subQ9=sQuery(id+"F0.wireOp",EDGE,"E1.left");var subQ10=sQuery(id+"F0.wireOp",EDGE,"E23.filletArc");var subQ11=sQuery(id+"F0.wireOp",EDGE,"E24.filletArc");Q0=makeQuery(id+"F2.boolean.opBoolean","SPLIT",FACE,{"disambiguationData":[TD([makeQuery(id+"F1.opExtrude","SWEPT_FACE",FACE,{"disambiguationData":[OSD([subQ6])]})])],"derivedFrom":makeQuery(id+"F1.opExtrude","CAP_FACE",FACE,{"disambiguationData":[OSD([subQ6,subQ8,subQ9,subQ7,subQ4,subQ3,subQ2,subQ1,subQ0,subQ5,subQ10,subQ11])],"isStart":true})});}
            var sketch = newSketch(context, id + "F16", { "sketchPlane" : qUnion([Q0])});
            skLineSegment(sketch, "E79", {"start": v(0, 74.25) * mm, "end": v(0, 104.25) * mm, "construction": true});
            skCircle(sketch, "E80", {"center": v(0, 104.25) * mm, "radius": 6 * mm});
            skLineSegment(sketch, "E81", {"start": v(-15, 104.25) * mm, "end": v(-15, 92.25) * mm});
            skLineSegment(sketch, "E82", {"start": v(15, 104.25) * mm, "end": v(15, 92.25) * mm});
            skArc(sketch, "E83", {"start": v(15, 104.25) * mm, "mid": v(0, 119.25) * mm, "end": v(-15, 104.25) * mm});
            skLineSegment(sketch, "E84", {"start": v(15, 92.25) * mm, "end": v(33, 74.25) * mm});
            skLineSegment(sketch, "E85", {"start": v(-15, 92.25) * mm, "end": v(-33, 74.25) * mm});
            skLineSegment(sketch, "E86", {"start": v(-88.12, 0) * mm, "end": v(98.59, 0) * mm, "construction": true});
            skPoint(sketch, "E86.startSnap0", {"position": v(-74.25, 0) * mm});
            skPoint(sketch, "E86.endSnap0", {"position": v(-74.25, 0) * mm});
            skLineSegment(sketch, "E87.MirrorCS", {"start": v(-15, -92.25) * mm, "end": v(-33, -74.25) * mm});
            skLineSegment(sketch, "E88.MirrorCS", {"start": v(-15, -104.25) * mm, "end": v(-15, -92.25) * mm});
            skArc(sketch, "E89.MirrorCS", {"start": v(15, -104.25) * mm, "mid": v(0, -119.25) * mm, "end": v(-15, -104.25) * mm});
            skCircle(sketch, "E90.MirrorC", {"center": v(0, -104.25) * mm, "radius": 6 * mm});
            skLineSegment(sketch, "E91.MirrorCS", {"start": v(0, -74.25) * mm, "end": v(0, -104.25) * mm, "construction": true});
            skLineSegment(sketch, "E92.MirrorCS", {"start": v(15, -104.25) * mm, "end": v(15, -92.25) * mm});
            skLineSegment(sketch, "E93.MirrorCS", {"start": v(15, -92.25) * mm, "end": v(33, -74.25) * mm});
            skLineSegment(sketch, "E94", {"start": v(-74.25, 64.25) * mm, "end": v(-74.25, -64.25) * mm});
            skLineSegment(sketch, "E95", {"start": v(-64.25, -74.25) * mm, "end": v(-33, -74.25) * mm});
            skLineSegment(sketch, "E96", {"start": v(33, -74.25) * mm, "end": v(64.25, -74.25) * mm});
            skLineSegment(sketch, "E97", {"start": v(74.25, -64.25) * mm, "end": v(74.25, 64.25) * mm});
            skLineSegment(sketch, "E98", {"start": v(-64.25, 74.25) * mm, "end": v(-33, 74.25) * mm});
            skLineSegment(sketch, "E99", {"start": v(33, 74.25) * mm, "end": v(64.25, 74.25) * mm});
            skArc(sketch, "E100", {"start": v(-64.25, 74.25) * mm, "mid": v(-71.32, 71.32) * mm, "end": v(-74.25, 64.25) * mm});
            skArc(sketch, "E101", {"start": v(74.25, 64.25) * mm, "mid": v(71.32, 71.32) * mm, "end": v(64.25, 74.25) * mm});
            skArc(sketch, "E102", {"start": v(-74.25, -64.25) * mm, "mid": v(-71.32, -71.32) * mm, "end": v(-64.25, -74.25) * mm});
            skArc(sketch, "E103", {"start": v(64.25, -74.25) * mm, "mid": v(71.32, -71.32) * mm, "end": v(74.25, -64.25) * mm});
            skArc(sketch, "E104", {"start": v(54.26, 47.88) * mm, "mid": v(0, 59.74) * mm, "end": v(-54.26, 47.88) * mm});
            skArc(sketch, "E105", {"start": v(-54.26, -47.88) * mm, "mid": v(0, -59.74) * mm, "end": v(54.26, -47.88) * mm});
            skLineSegment(sketch, "E106", {"start": v(-60, 38.83) * mm, "end": v(-60, -38.83) * mm});
            skLineSegment(sketch, "E107", {"start": v(60, 38.83) * mm, "end": v(60, -38.83) * mm});
            skArc(sketch, "E108", {"start": v(-54.26, 47.88) * mm, "mid": v(-58.44, 44.2) * mm, "end": v(-60, 38.83) * mm});
            skArc(sketch, "E109", {"start": v(60, 38.83) * mm, "mid": v(58.44, 44.2) * mm, "end": v(54.26, 47.88) * mm});
            skArc(sketch, "E110", {"start": v(54.26, -47.88) * mm, "mid": v(58.44, -44.2) * mm, "end": v(60, -38.83) * mm});
            skArc(sketch, "E111", {"start": v(-60, -38.83) * mm, "mid": v(-58.44, -44.2) * mm, "end": v(-54.26, -47.88) * mm});
            skCircle(sketch, "E112", {"center": v(-60, -60) * mm, "radius": 3.65 * mm});
            skCircle(sketch, "E113", {"center": v(-60, 60) * mm, "radius": 3.99 * mm});
            skCircle(sketch, "E114", {"center": v(60, 60) * mm, "radius": 3.69 * mm});
            skCircle(sketch, "E115", {"center": v(60, -60) * mm, "radius": 3.57 * mm});
            skSolve(sketch);
        }
        {
            var Q0;
            Q0 = qSketchRegion(id + "F16", true);
            extrude(context, id + "F17", {"entities" : qUnion([Q0]), "depth" : 5 * mm});
        }
    });
